# Revit family: Electrical-Box_FSR_TB-6G
name_source: partatom
category: Electrical Fixtures
units: mm (PartAtom-declared; Revit-internal decimal feet)

## family parameters
Always vertical = Yes
Classification Number = 23.85.10.17.11
Cut with Voids When Loaded = No
Maintain Annotation Orientation = No
Part Type = Normal
Room Calculation Point = No
Round Connector Dimension = Use Diameter
Shared = No
Work Plane-Based = Yes

## types (8) — shared parameters
Al = 6 "
An = 7 "
Assembly Code = D5020100
Body Material = Material and Finish as Specified in 26 27 26
Construction Details = ftp://doclib.fsrinc.com/
Default Elevation = 48 "
Device 1 = Device : AC Power Outlet
Device 2 = Device : Device As Specified
Device 3 = Device : Device As Specified
Device 4 = Device : Device As Specified
Device 5 = Device : Device As Specified
Device 6 = Device : Device As Specified
Green Building-LEED = http://www.arcat.com
Installation_Fabricaton = ftp://doclib.fsrinc.com/
Keynote = 26 27 26
La = 10 "
Manufacturer = FSR Inc.
Manufacturer Fax = 973-785-4207
Manufacturer Website = http://www.fsrinc.com
Model = TB-6G
Product Data = http://www.arcat.com
Sales Information = http://www.fsrinc.com
Send Message = http://admin.arcat.com
Specification = http://www.arcat.com
Test Data = ftp://doclib.fsrinc.com/
URL = http://www.fsrinc.com
zero-valued in all types: Expected Lifespan (Years), Maintenance Schedule (Months), Warranty Duration (Years)

## per-type parameters (varying)
| type | Cover Material | Description |
| Custom Wood Cover - Cable Lift - Supplied by Others | Wood As Specified | FSR TB-6G - Custom Wood Cover - Cable Lift - Supplied by Others |
| Brass Cover - Cable Lift | Brass | FSR TB-6G - Brass Cover - Cable Lift |
| Aluminum Cover - Cable Lift | Aluminum | FSR TB-6G - Aluminum Cover - Cable Lift |
| Black Cover - Cable Lift | Black | FSR TB-6G - Black Cover - Cable Lift |
| Custom Wood Cover - Spring Lift - Supplied by Others | Wood As Specified | FSR TB-6G - Custom Wood Cover - Spring Lift - Supplied by Others |
| Brass Cover - Spring Lift | Brass | FSR TB-6G - Brass Cover - Spring Lift |
| Aluminum Cover - Spring Lift | Aluminum | FSR TB-6G - Aluminum Cover - Spring Lift |
| Black Cover - Spring Lift | Black | FSR TB-6G - Black Cover - Spring Lift |

## geometry (parser evidence)
native form markers: Blend x18, Sweep x6
no freeform markers — native parametric forms only
